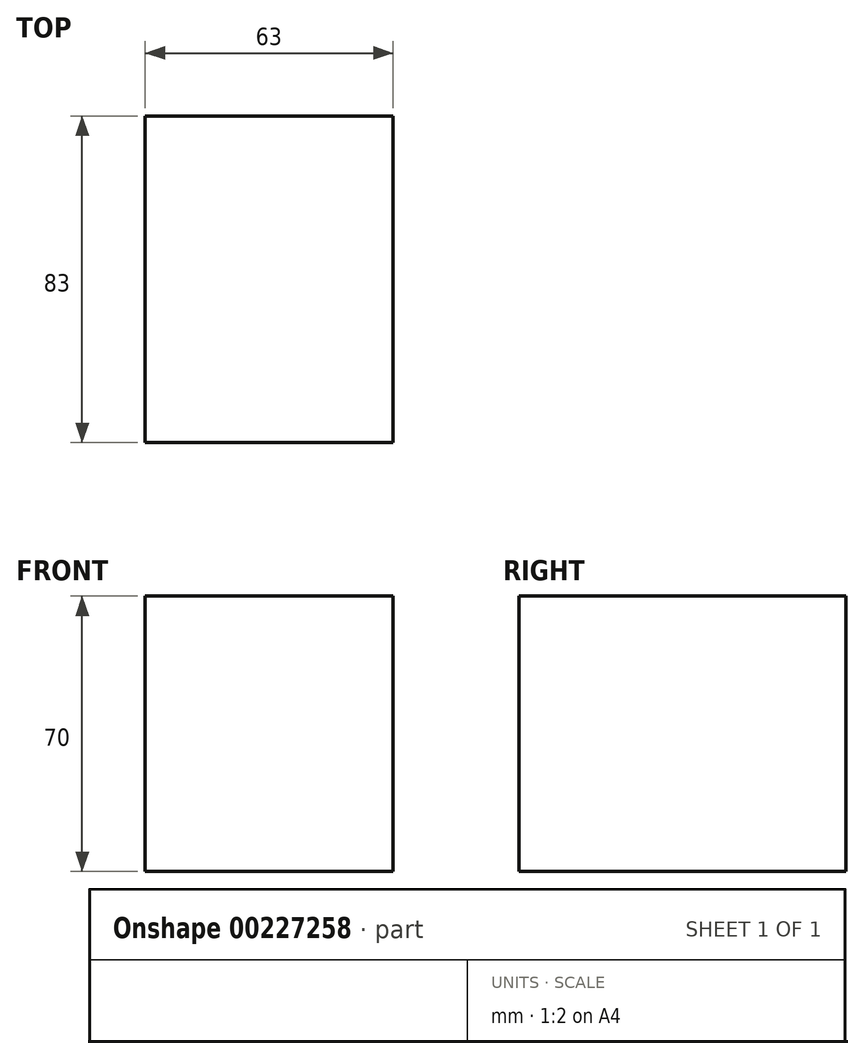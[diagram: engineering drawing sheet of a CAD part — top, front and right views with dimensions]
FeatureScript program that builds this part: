
annotation { "Feature Type Name" : "Feature", "Feature Type Description" : "" }
export const myFeature = defineFeature(function(context is Context, id is Id, definition is map)
    precondition{}
    {
        {
            var Q0;
            Q0=qCreatedBy(makeId("Top.planeOp"),FACE);
            var sketch = newSketch(context, id + "F0", { "sketchPlane" : qUnion([Q0])});
            skLineSegment(sketch, "E0.bottom", {"start": v(31.5, -41.5) * mm, "end": v(-31.5, -41.5) * mm});
            skLineSegment(sketch, "E0.top", {"start": v(31.5, 41.5) * mm, "end": v(-31.5, 41.5) * mm});
            skLineSegment(sketch, "E0.left", {"start": v(31.5, -41.5) * mm, "end": v(31.5, 41.5) * mm});
            skLineSegment(sketch, "E0.right", {"start": v(-31.5, -41.5) * mm, "end": v(-31.5, 41.5) * mm});
            skPoint(sketch, "E0.middle", {"position": v(0, 0) * mm});
            skSolve(sketch);
        }
        {
            var Q0;
            Q0 = qSketchRegion(id + "F0", true);
            extrude(context, id + "F1", {"entities" : qUnion([Q0]), "depth" : 70 * mm});
        }
    });
